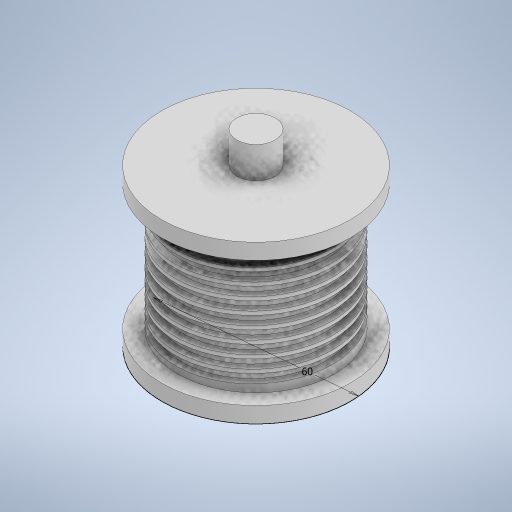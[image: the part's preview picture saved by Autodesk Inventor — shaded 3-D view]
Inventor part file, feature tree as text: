
AUTODESK INVENTOR PART (.ipt)
format: ipt  version: 2024 (Build 280153000, 153)  size: 1,281,536 bytes
history: native  units: mm
features: sketch x11, extrude x8, other x3, revolve x1, projected_geometry x1
ambient origin geometry x8: Origin, YZ Plane, XZ Plane, XY Plane, X Axis, Y Axis, Z Axis, Center Point
bodies: Body1 (feature_tree)
feature tree (24):
  other  "Sólido1"
  extrude  "Extrusión1"  Depth=50.0mm TaperAngle=0.0deg
  revolve  "Revolución1"  [1 undecoded]
  other  "Bobina1"
  extrude  "Extrusión2"  TaperAngle=90.0deg  [1 undecoded]
  other  "Bobina2"
  extrude  "Extrusión3"  Depth=2.0mm
  extrude  "Extrusión5"  Depth=2.0mm
  extrude  "Extrusión6"  Depth=5.0mm TaperAngle=0.0deg
  extrude  "Extrusión4"  Depth=16.0mm
  extrude  "Extrusión7"  Depth=1.0mm
  extrude  "Extrusión8"  Depth=2.0mm
  sketch  "Boceto1"  dims[d0=60.0mm d1=50.0mm d2=0.0mm]
  sketch  "Boceto2"  dims[d3=5.0mm d4=5.0mm]
  sketch  "Boceto3"  dims[d5=40.0mm d6=90.0deg]
  sketch  "Boceto4"  dims[d8=2.0mm d11=0.5mm]
  projected_geometry  "Contorno proyectado1"
  sketch  "Boceto5"  dims[d12=2.0mm d14=3.328427mm]
  sketch  "Boceto7"  dims[d15=4.0mm d16=10.0mm d17=95.0mm d18=0.0mm d19=90.0deg d20=90.0deg d21=0.0mm d22=0.0mm d23=5.0mm d24=0.0mm]
  sketch  "Boceto8"  dims[d25=16.0mm d26=0.0mm d30=0.5mm]
  sketch  "Boceto9"  dims[d31=180.0deg d32=1.0mm]
  sketch  "Boceto11"  dims[d33=0.5mm d34=2.0mm]
  sketch  "Boceto12"  dims[d35=90.0deg]
  sketch  "Boceto13"  dims[d39=0.5mm d40=1.0mm d41=90.0deg d42=2.0mm d43=4.0mm d44=10.0mm d45=95.0mm d46=0.0mm d47=90.0deg d48=90.0deg d49=0.0mm d50=0.0mm d51=2.2mm d52=10.0mm d53=0.0mm d56=2.5mm d57=1.0mm d58=180.0deg d59=2.0mm d60=10.0mm d61=0.0mm d62=8.0mm d63=10.0mm d64=0.0mm d65=16.0mm d66=0.0mm d67=10.0mm d68=0.0mm d69=7.9mm d70=12.2mm d71=10.0mm d72=0.0mm]
note: 2 required parameter values undecoded (feature->parameter linkage not recoverable at this tier; creation-order binding heuristic only, values carry confidence <= 0.55)